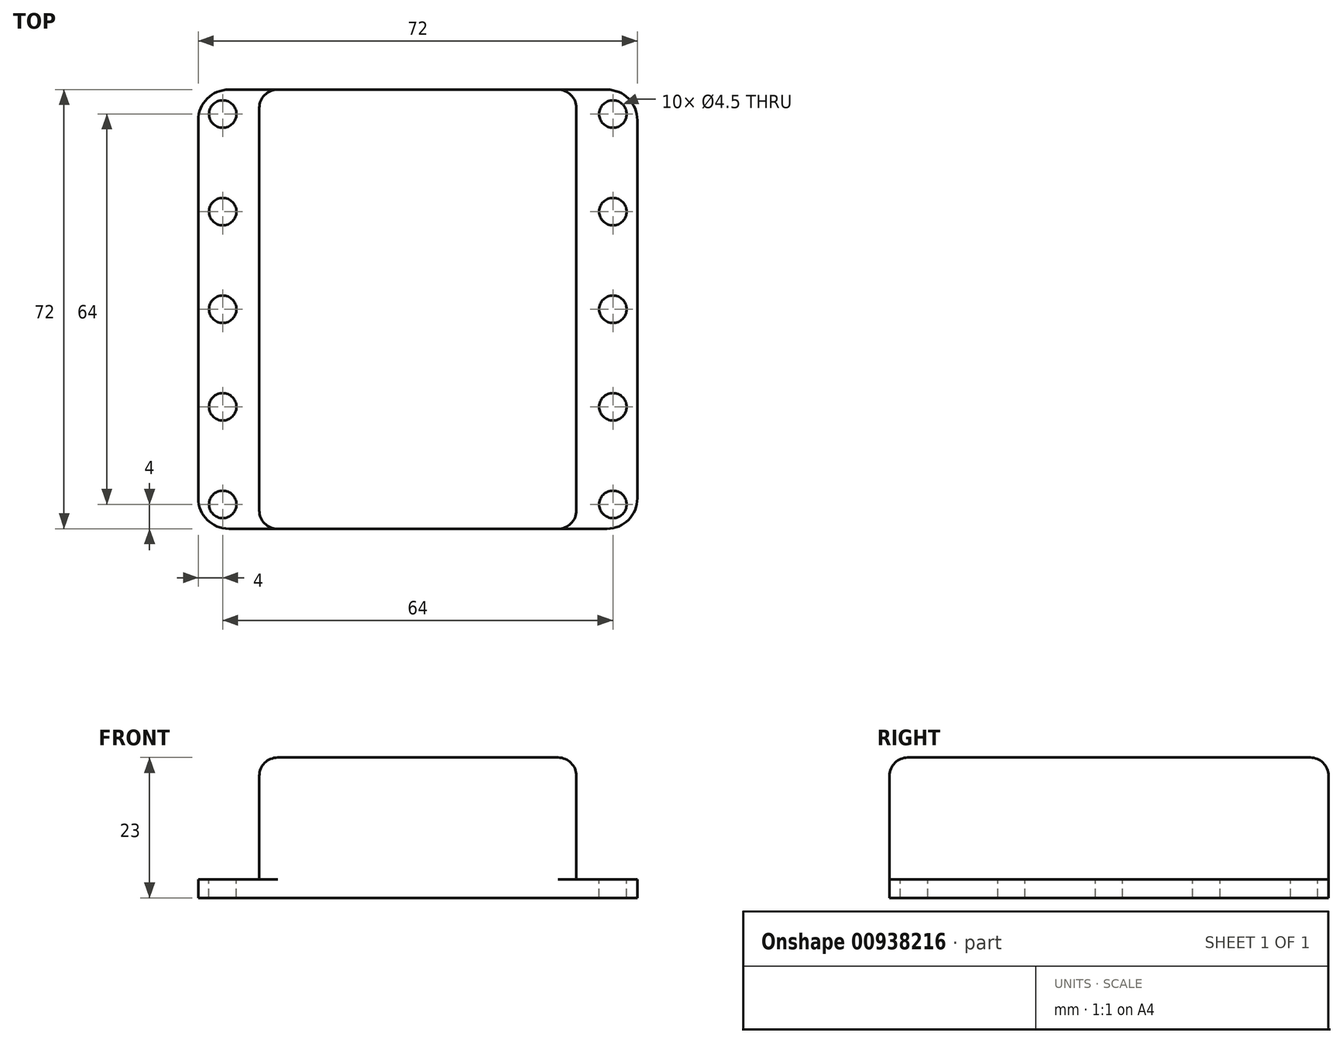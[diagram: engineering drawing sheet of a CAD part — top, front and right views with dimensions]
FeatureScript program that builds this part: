
annotation { "Feature Type Name" : "Feature", "Feature Type Description" : "" }
export const myFeature = defineFeature(function(context is Context, id is Id, definition is map)
    precondition{}
    {
        {
            var Q0;
            Q0=qCreatedBy(makeId("Top.planeOp"),FACE);
            var sketch = newSketch(context, id + "F0", { "sketchPlane" : qUnion([Q0])});
            skLineSegment(sketch, "E0.bottom", {"start": v(36, -36) * mm, "end": v(-36, -36) * mm});
            skLineSegment(sketch, "E0.top", {"start": v(36, 36) * mm, "end": v(-36, 36) * mm});
            skLineSegment(sketch, "E0.left", {"start": v(36, -36) * mm, "end": v(36, 36) * mm});
            skLineSegment(sketch, "E0.right", {"start": v(-36, -36) * mm, "end": v(-36, 36) * mm});
            skPoint(sketch, "E0.middle", {"position": v(0, 0) * mm});
            skSolve(sketch);
        }
        {
            var Q0;
            Q0=makeQuery(id+"F0.imprint","IMPRINT",FACE,{"disambiguationData":[TD([[makeQuery(id+"F0.imprint","IMPRINT",EDGE,{"derivedFrom":sQuery(id+"F0.wireOp",EDGE,"E0.bottom")}),-1.0]])]});
            extrude(context, id + "F1", {"entities" : qUnion([Q0]), "depth" : 3 * mm});
        }
        {
            var Q0;
            Q0=makeQuery(id+"F1.opExtrude","CAP_FACE",FACE,{"disambiguationData":[OSD([sQuery(id+"F0.wireOp",EDGE,"E0.bottom"),sQuery(id+"F0.wireOp",EDGE,"E0.top"),sQuery(id+"F0.wireOp",EDGE,"E0.left"),sQuery(id+"F0.wireOp",EDGE,"E0.right")])],"isStart":false});
            var sketch = newSketch(context, id + "F2", { "sketchPlane" : qUnion([Q0])});
            skLineSegment(sketch, "E1.bottom", {"start": v(26, 36) * mm, "end": v(-26, 36) * mm});
            skLineSegment(sketch, "E1.top", {"start": v(26, -36) * mm, "end": v(-26, -36) * mm});
            skLineSegment(sketch, "E1.left", {"start": v(26, 36) * mm, "end": v(26, -36) * mm});
            skLineSegment(sketch, "E1.right", {"start": v(-26, 36) * mm, "end": v(-26, -36) * mm});
            skPoint(sketch, "E1.middle", {"position": v(0, 0) * mm});
            skSolve(sketch);
        }
        {
            var Q0;
            Q0=makeQuery(id+"F2.imprint","IMPRINT",FACE,{"disambiguationData":[TD([[makeQuery(id+"F2.imprint","IMPRINT",EDGE,{"derivedFrom":sQuery(id+"F2.wireOp",EDGE,"E1.bottom")}),1.0]])]});
            extrude(context, id + "F3", {"entities" : qUnion([Q0]), "operationType" : NewBodyOperationType.ADD, "depth" : 20 * mm});
        }
        {
            var Q0;
            {var subQ0=sQuery(id+"F0.wireOp",EDGE,"E0.left");var subQ1=sQuery(id+"F0.wireOp",EDGE,"E0.top");var subQ2=sQuery(id+"F0.wireOp",EDGE,"E0.bottom");Q0=makeQuery(id+"F3.boolean.opBoolean","SPLIT",FACE,{"disambiguationData":[TD([makeQuery(id+"F1.opExtrude","SWEPT_FACE",FACE,{"disambiguationData":[OSD([subQ0])]})])],"derivedFrom":makeQuery(id+"F1.opExtrude","CAP_FACE",FACE,{"disambiguationData":[OSD([subQ2,subQ1,subQ0,sQuery(id+"F0.wireOp",EDGE,"E0.right")])],"isStart":false})});}
            var sketch = newSketch(context, id + "F4", { "sketchPlane" : qUnion([Q0])});
            skPoint(sketch, "E2", {"position": v(32, -32) * mm});
            skPoint(sketch, "E3", {"position": v(32, -16) * mm});
            skPoint(sketch, "E4", {"position": v(32, 0) * mm});
            skPoint(sketch, "E5", {"position": v(32, 16) * mm});
            skPoint(sketch, "E6", {"position": v(32, 32) * mm});
            skSolve(sketch);
        }
        {
            var Q0;
            Q0=sQuery(id+"F4.wireOp",VERTEX,"E6");
            var Q1;
            Q1=sQuery(id+"F4.wireOp",VERTEX,"E5");
            var Q2;
            Q2=sQuery(id+"F4.wireOp",VERTEX,"E4");
            var Q3;
            Q3=sQuery(id+"F4.wireOp",VERTEX,"E3");
            var Q4;
            Q4=sQuery(id+"F4.wireOp",VERTEX,"E2");
            var Q5;
            Q5=makeQuery(id+"F1.opExtrude","SWEPT_BODY",BODY,{"disambiguationData":[OSD([sQuery(id+"F0.wireOp",EDGE,"E0.bottom"),sQuery(id+"F0.wireOp",EDGE,"E0.top"),sQuery(id+"F0.wireOp",EDGE,"E0.left"),sQuery(id+"F0.wireOp",EDGE,"E0.right")])]});
            hole(context, id + "F5", {"style" : HoleStyle.SIMPLE, "endStyle" : HoleEndStyle.THROUGH, "holeDiameter" : 4.5 * mm, "locations" : qUnion([Q0, Q1, Q2, Q3, Q4]), "scope" : qUnion([Q5]), "isTappedThrough" : true});
        }
        {
            var Q0;
            {var subQ0=sQuery(id+"F0.wireOp",EDGE,"E0.right");var subQ1=sQuery(id+"F0.wireOp",EDGE,"E0.top");var subQ2=sQuery(id+"F0.wireOp",EDGE,"E0.bottom");Q0=makeQuery(id+"F3.boolean.opBoolean","SPLIT",FACE,{"disambiguationData":[TD([makeQuery(id+"F1.opExtrude","SWEPT_FACE",FACE,{"disambiguationData":[OSD([subQ0])]})])],"derivedFrom":makeQuery(id+"F1.opExtrude","CAP_FACE",FACE,{"disambiguationData":[OSD([subQ2,subQ1,sQuery(id+"F0.wireOp",EDGE,"E0.left"),subQ0])],"isStart":false})});}
            var sketch = newSketch(context, id + "F6", { "sketchPlane" : qUnion([Q0])});
            skPoint(sketch, "E7", {"position": v(-32, 32) * mm});
            skPoint(sketch, "E8", {"position": v(-32, 16) * mm});
            skPoint(sketch, "E9", {"position": v(-32, 0) * mm});
            skPoint(sketch, "E10", {"position": v(-32, -16) * mm});
            skPoint(sketch, "E11", {"position": v(-32, -32) * mm});
            skSolve(sketch);
        }
        {
            var Q0;
            Q0=sQuery(id+"F6.wireOp",VERTEX,"E7");
            var Q1;
            Q1=sQuery(id+"F6.wireOp",VERTEX,"E8");
            var Q2;
            Q2=sQuery(id+"F6.wireOp",VERTEX,"E9");
            var Q3;
            Q3=sQuery(id+"F6.wireOp",VERTEX,"E10");
            var Q4;
            Q4=sQuery(id+"F6.wireOp",VERTEX,"E11");
            var Q5;
            Q5=makeQuery(id+"F1.opExtrude","SWEPT_BODY",BODY,{"disambiguationData":[OSD([sQuery(id+"F0.wireOp",EDGE,"E0.bottom"),sQuery(id+"F0.wireOp",EDGE,"E0.top"),sQuery(id+"F0.wireOp",EDGE,"E0.left"),sQuery(id+"F0.wireOp",EDGE,"E0.right")])]});
            hole(context, id + "F7", {"style" : HoleStyle.SIMPLE, "endStyle" : HoleEndStyle.THROUGH, "holeDiameter" : 4.5 * mm, "locations" : qUnion([Q0, Q1, Q2, Q3, Q4]), "scope" : qUnion([Q5]), "isTappedThrough" : true});
        }
        {
            var Q0;
            Q0=makeQuery(id+"F1.opExtrude","SWEPT_EDGE",EDGE,{"disambiguationData":[OSD([sQuery(id+"F0.wireOp",EDGE,"E0.top"),sQuery(id+"F0.wireOp",EDGE,"E0.right")])]});
            var Q1;
            Q1=makeQuery(id+"F1.opExtrude","SWEPT_EDGE",EDGE,{"disambiguationData":[OSD([sQuery(id+"F0.wireOp",EDGE,"E0.bottom"),sQuery(id+"F0.wireOp",EDGE,"E0.right")])]});
            var Q2;
            Q2=makeQuery(id+"F1.opExtrude","SWEPT_EDGE",EDGE,{"disambiguationData":[OSD([sQuery(id+"F0.wireOp",EDGE,"E0.bottom"),sQuery(id+"F0.wireOp",EDGE,"E0.left")])]});
            var Q3;
            Q3=makeQuery(id+"F1.opExtrude","SWEPT_EDGE",EDGE,{"disambiguationData":[OSD([sQuery(id+"F0.wireOp",EDGE,"E0.top"),sQuery(id+"F0.wireOp",EDGE,"E0.left")])]});
            fillet(context, id + "F8", {"entities" : qUnion([Q0, Q1, Q2, Q3]), "radius" : 5 * mm, "tangentPropagation" : true, "allowEdgeOverflow" : false});
        }
        {
            var Q0;
            Q0=makeQuery(id+"F3.opExtrude","SWEPT_EDGE",EDGE,{"disambiguationData":[OSD([sQuery(id+"F0.wireOp",EDGE,"E0.bottom"),sQuery(id+"F2.wireOp",EDGE,"E1.top"),sQuery(id+"F2.wireOp",EDGE,"E1.right")])]});
            var Q1;
            Q1=makeQuery(id+"F3.opExtrude","SWEPT_EDGE",EDGE,{"disambiguationData":[OSD([sQuery(id+"F0.wireOp",EDGE,"E0.bottom"),sQuery(id+"F2.wireOp",EDGE,"E1.top"),sQuery(id+"F2.wireOp",EDGE,"E1.left")])]});
            var Q2;
            Q2=makeQuery(id+"F3.opExtrude","CAP_EDGE",EDGE,{"disambiguationData":[OSD([sQuery(id+"F2.wireOp",EDGE,"E1.top")])],"isStart":false});
            var Q3;
            Q3=makeQuery(id+"F3.opExtrude","CAP_EDGE",EDGE,{"disambiguationData":[OSD([sQuery(id+"F2.wireOp",EDGE,"E1.right")])],"isStart":false});
            var Q4;
            Q4=makeQuery(id+"F3.opExtrude","CAP_EDGE",EDGE,{"disambiguationData":[OSD([sQuery(id+"F2.wireOp",EDGE,"E1.bottom")])],"isStart":false});
            var Q5;
            Q5=makeQuery(id+"F3.opExtrude","CAP_EDGE",EDGE,{"disambiguationData":[OSD([sQuery(id+"F2.wireOp",EDGE,"E1.left")])],"isStart":false});
            var Q6;
            Q6=makeQuery(id+"F3.opExtrude","SWEPT_EDGE",EDGE,{"disambiguationData":[OSD([sQuery(id+"F0.wireOp",EDGE,"E0.top"),sQuery(id+"F2.wireOp",EDGE,"E1.bottom"),sQuery(id+"F2.wireOp",EDGE,"E1.left")])]});
            var Q7;
            Q7=makeQuery(id+"F3.opExtrude","SWEPT_EDGE",EDGE,{"disambiguationData":[OSD([sQuery(id+"F0.wireOp",EDGE,"E0.top"),sQuery(id+"F2.wireOp",EDGE,"E1.bottom"),sQuery(id+"F2.wireOp",EDGE,"E1.right")])]});
            fillet(context, id + "F9", {"entities" : qUnion([Q0, Q1, Q2, Q3, Q4, Q5, Q6, Q7]), "radius" : 3 * mm, "tangentPropagation" : true, "allowEdgeOverflow" : false});
        }
    });
